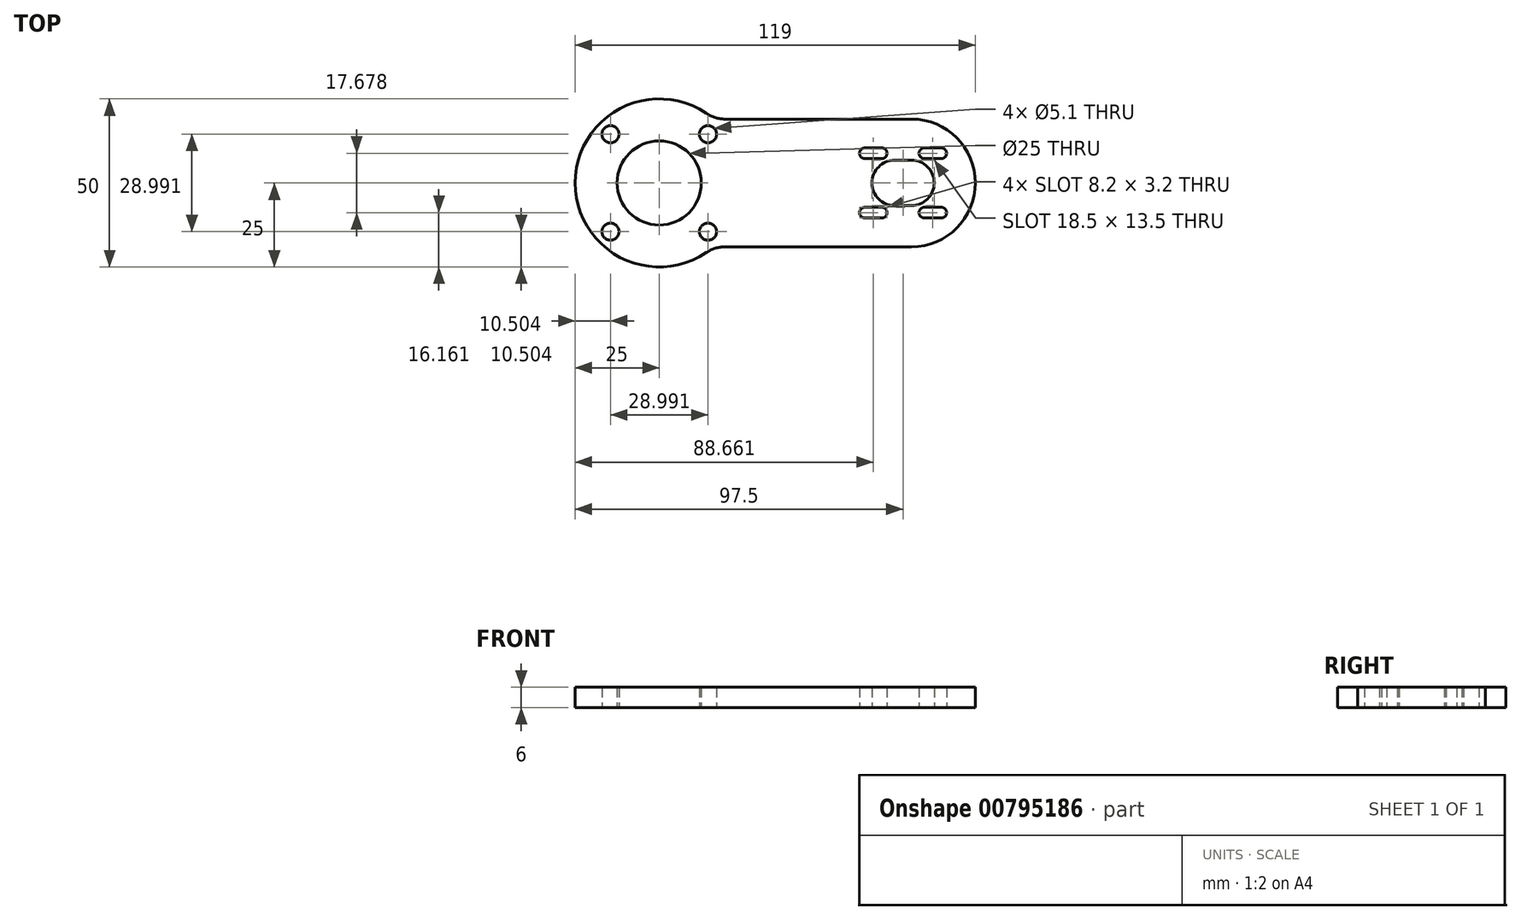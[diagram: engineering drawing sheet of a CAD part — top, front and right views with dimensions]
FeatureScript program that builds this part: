
annotation { "Feature Type Name" : "Feature", "Feature Type Description" : "" }
export const myFeature = defineFeature(function(context is Context, id is Id, definition is map)
    precondition{}
    {
        {
            var Q0;
            Q0=qCreatedBy(makeId("Top.planeOp"),FACE);
            var sketch = newSketch(context, id + "F0", { "sketchPlane" : qUnion([Q0])});
            skCircle(sketch, "E0", {"center": v(0, 0) * mm, "radius": 12.5 * mm});
            skArc(sketch, "E1", {"start": v(14, 20.71) * mm, "mid": v(-25, 0) * mm, "end": v(14, -20.71) * mm});
            skLineSegment(sketch, "E2.left", {"start": v(0, 25) * mm, "end": v(0, -25) * mm, "construction": true});
            skLineSegment(sketch, "E2.right", {"start": v(90, 25) * mm, "end": v(90, -25) * mm});
            skLineSegment(sketch, "E3", {"start": v(0, 0) * mm, "end": v(77.4, 0) * mm, "construction": true});
            skCircle(sketch, "E4", {"center": v(70, 0) * mm, "radius": 6.75 * mm, "construction": true});
            skCircle(sketch, "E5", {"center": v(70, 0) * mm, "radius": 19 * mm, "construction": true});
            skLineSegment(sketch, "E6.bottom", {"start": v(45.4, -41.12) * mm, "end": v(-45.4, -41.12) * mm, "construction": true});
            skLineSegment(sketch, "E6.top", {"start": v(45.4, 41.12) * mm, "end": v(-45.4, 41.12) * mm, "construction": true});
            skLineSegment(sketch, "E6.right", {"start": v(-45.4, -41.12) * mm, "end": v(-45.4, 41.12) * mm, "construction": true});
            skCircle(sketch, "E7", {"center": v(70, 0) * mm, "radius": 6.75 * mm});
            skLineSegment(sketch, "E8", {"start": v(70, 0) * mm, "end": v(61.16, 8.84) * mm, "construction": true});
            skCircle(sketch, "E9", {"center": v(61.16, 8.84) * mm, "radius": 1.6 * mm});
            skCircle(sketch, "E10.1.0", {"center": v(61.16, -8.84) * mm, "radius": 1.6 * mm});
            skCircle(sketch, "E10.2.0", {"center": v(78.84, -8.84) * mm, "radius": 1.6 * mm});
            skCircle(sketch, "E10.3.0", {"center": v(78.84, 8.84) * mm, "radius": 1.6 * mm});
            skLineSegment(sketch, "E11", {"start": v(61.16, 8.84) * mm, "end": v(66.16, 8.84) * mm});
            skLineSegment(sketch, "E12", {"start": v(61.16, -8.84) * mm, "end": v(66.16, -8.84) * mm});
            skLineSegment(sketch, "E13", {"start": v(78.84, -8.84) * mm, "end": v(83.84, -8.84) * mm});
            skLineSegment(sketch, "E14", {"start": v(78.84, 8.84) * mm, "end": v(83.84, 8.84) * mm});
            skLineSegment(sketch, "E15", {"start": v(70, 0) * mm, "end": v(75, 0) * mm});
            skArc(sketch, "E16.0.startCap", {"start": v(78.84, 7.24) * mm, "mid": v(77.24, 8.84) * mm, "end": v(78.84, 10.44) * mm});
            skArc(sketch, "E16.0.endCap", {"start": v(83.84, 10.44) * mm, "mid": v(85.44, 8.84) * mm, "end": v(83.84, 7.24) * mm});
            skLineSegment(sketch, "E16.0.left", {"start": v(78.84, 10.44) * mm, "end": v(83.84, 10.44) * mm});
            skLineSegment(sketch, "E16.0.right", {"start": v(78.84, 7.24) * mm, "end": v(83.84, 7.24) * mm});
            skArc(sketch, "E17.0.startCap", {"start": v(61.16, 7.24) * mm, "mid": v(59.56, 8.84) * mm, "end": v(61.16, 10.44) * mm});
            skArc(sketch, "E17.0.endCap", {"start": v(66.16, 10.44) * mm, "mid": v(67.76, 8.84) * mm, "end": v(66.16, 7.24) * mm});
            skLineSegment(sketch, "E17.0.left", {"start": v(61.16, 10.44) * mm, "end": v(66.16, 10.44) * mm});
            skLineSegment(sketch, "E17.0.right", {"start": v(61.16, 7.24) * mm, "end": v(66.16, 7.24) * mm});
            skArc(sketch, "E17.1.startCap", {"start": v(61.16, -10.44) * mm, "mid": v(59.56, -8.84) * mm, "end": v(61.16, -7.24) * mm});
            skArc(sketch, "E17.1.endCap", {"start": v(66.16, -7.24) * mm, "mid": v(67.76, -8.84) * mm, "end": v(66.16, -10.44) * mm});
            skLineSegment(sketch, "E17.1.left", {"start": v(61.16, -7.24) * mm, "end": v(66.16, -7.24) * mm});
            skLineSegment(sketch, "E17.1.right", {"start": v(61.16, -10.44) * mm, "end": v(66.16, -10.44) * mm});
            skArc(sketch, "E17.2.startCap", {"start": v(78.84, -10.44) * mm, "mid": v(77.24, -8.84) * mm, "end": v(78.84, -7.24) * mm});
            skArc(sketch, "E17.2.endCap", {"start": v(83.84, -7.24) * mm, "mid": v(85.44, -8.84) * mm, "end": v(83.84, -10.44) * mm});
            skLineSegment(sketch, "E17.2.left", {"start": v(78.84, -7.24) * mm, "end": v(83.84, -7.24) * mm});
            skLineSegment(sketch, "E17.2.right", {"start": v(78.84, -10.44) * mm, "end": v(83.84, -10.44) * mm});
            skArc(sketch, "E18.0.startCap", {"start": v(70, -6.75) * mm, "mid": v(63.25, 0) * mm, "end": v(70, 6.75) * mm});
            skArc(sketch, "E18.0.endCap", {"start": v(75, 6.75) * mm, "mid": v(81.75, 0) * mm, "end": v(75, -6.75) * mm});
            skLineSegment(sketch, "E18.0.left", {"start": v(70, 6.75) * mm, "end": v(75, 6.75) * mm});
            skLineSegment(sketch, "E18.0.right", {"start": v(70, -6.75) * mm, "end": v(75, -6.75) * mm});
            skArc(sketch, "E19", {"start": v(75, -19) * mm, "mid": v(94, 0) * mm, "end": v(75, 19) * mm});
            skLineSegment(sketch, "E20", {"start": v(75, 19) * mm, "end": v(19.6, 19) * mm});
            skLineSegment(sketch, "E21", {"start": v(75, -19) * mm, "end": v(19.6, -19) * mm});
            skPoint(sketch, "E22.visualSharp", {"position": v(16.25, 19) * mm});
            skArc(sketch, "E22.filletArc", {"start": v(14, 20.71) * mm, "mid": v(16.67, 19.44) * mm, "end": v(19.6, 19) * mm});
            skArc(sketch, "E23.filletArc", {"start": v(19.6, -19) * mm, "mid": v(16.67, -19.44) * mm, "end": v(14, -20.71) * mm});
            skCircle(sketch, "E24", {"center": v(0, 0) * mm, "radius": 20.5 * mm, "construction": true});
            skCircle(sketch, "E25", {"center": v(0, 0) * mm, "radius": 16 * mm, "construction": true});
            skLineSegment(sketch, "E26", {"start": v(0, 0) * mm, "end": v(-28.53, 28.53) * mm, "construction": true});
            skCircle(sketch, "E27", {"center": v(-14.5, 14.5) * mm, "radius": 2.55 * mm});
            skCircle(sketch, "E28.1.0", {"center": v(-14.5, -14.5) * mm, "radius": 2.55 * mm});
            skCircle(sketch, "E28.2.0", {"center": v(14.5, -14.5) * mm, "radius": 2.55 * mm});
            skCircle(sketch, "E28.3.0", {"center": v(14.5, 14.5) * mm, "radius": 2.55 * mm});
            skSolve(sketch);
        }
        {
            var Q0;
            Q0 = qSketchRegion(id + "F0", true);
            extrude(context, id + "F1", {"entities" : qUnion([Q0]), "depth" : 6 * mm, "offsetDistance" : 25 * mm});
        }
    });
